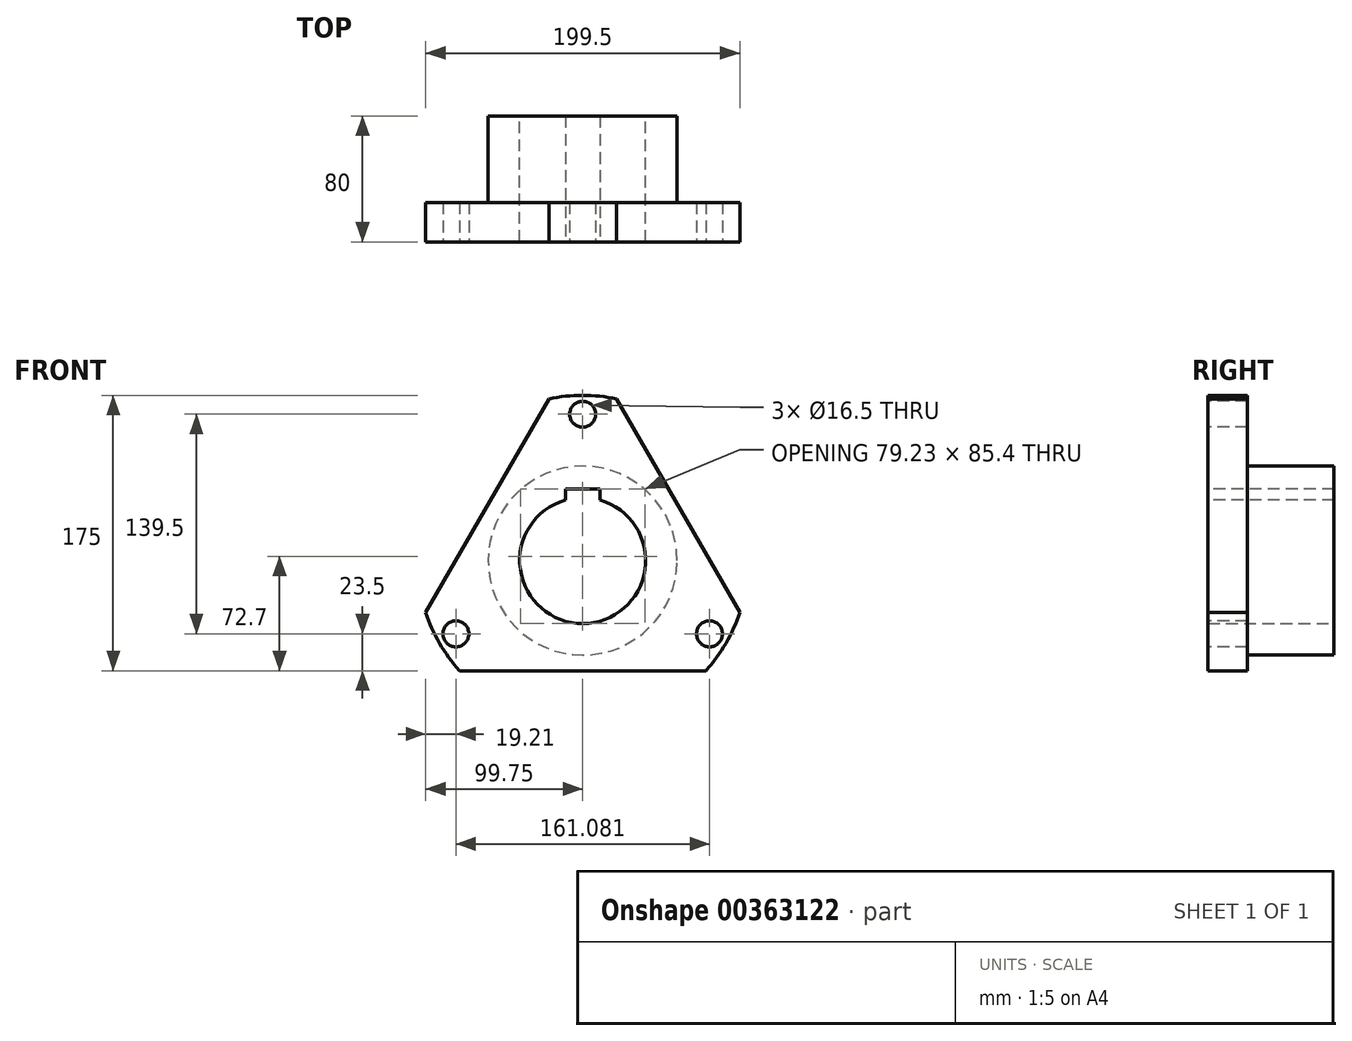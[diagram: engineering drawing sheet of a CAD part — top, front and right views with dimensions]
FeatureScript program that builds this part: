
annotation { "Feature Type Name" : "Feature", "Feature Type Description" : "" }
export const myFeature = defineFeature(function(context is Context, id is Id, definition is map)
    precondition{}
    {
        {
            var Q0;
            Q0=qCreatedBy(makeId("Front.planeOp"),FACE);
            var sketch = newSketch(context, id + "F0", { "sketchPlane" : qUnion([Q0])});
            skCircle(sketch, "E0", {"center": v(0, 0) * mm, "radius": 40 * mm});
            skCircle(sketch, "E1", {"center": v(0, 0) * mm, "radius": 60 * mm});
            skSolve(sketch);
        }
        {
            var Q0;
            Q0=qSketchRegion(id+"F0",true);
            extrude(context, id + "F1", {"entities" : qUnion([Q0]), "depth" : 80 * mm});
        }
        {
            var Q0;
            Q0=makeQuery(id+"F1.opExtrude","CAP_FACE",FACE,{"disambiguationData":[OSD([sQuery(id+"F0.wireOp",EDGE,"E0"),sQuery(id+"F0.wireOp",EDGE,"E1")])],"isStart":false});
            var sketch = newSketch(context, id + "F2", { "sketchPlane" : qUnion([Q0])});
            skCircle(sketch, "E2", {"center": v(0, 0) * mm, "radius": 105 * mm});
            skCircle(sketch, "E3", {"center": v(0, 0) * mm, "radius": 93 * mm, "construction": true});
            skCircle(sketch, "E4", {"center": v(0, 93) * mm, "radius": 8.25 * mm});
            skCircle(sketch, "E5.1.0", {"center": v(-80.54, -46.5) * mm, "radius": 8.25 * mm});
            skCircle(sketch, "E5.2.0", {"center": v(80.54, -46.5) * mm, "radius": 8.25 * mm});
            skLineSegment(sketch, "E6", {"start": v(-98.6, -61.27) * mm, "end": v(0, 109.5) * mm, "construction": true});
            skLineSegment(sketch, "E7", {"start": v(-99.75, -32.78) * mm, "end": v(-21.5, 102.78) * mm});
            skLineSegment(sketch, "E8.1.0", {"start": v(78.26, -70) * mm, "end": v(-78.26, -70) * mm});
            skLineSegment(sketch, "E8.2.0", {"start": v(21.5, 102.78) * mm, "end": v(99.75, -32.78) * mm});
            skSolve(sketch);
        }
        {
            var Q0;
            Q0=makeQuery(id+"F2.imprint","IMPRINT",FACE,{"disambiguationData":[TD([[makeQuery(id+"F2.imprint","IMPRINT",EDGE,{"derivedFrom":sQuery(id+"F2.wireOp",EDGE,"E4")}),-1.0]])]});
            var Q1;
            Q1=makeQuery(id+"F2.imprint","IMPRINT",FACE,{"disambiguationData":[TD([[makeQuery(id+"F2.imprint","IMPRINT",EDGE,{"derivedFrom":sQuery(id+"F2.wireOp",EDGE,"E5.1.0")}),-1.0]])]});
            var Q2;
            Q2=makeQuery(id+"F2.imprint","IMPRINT",FACE,{"disambiguationData":[TD([[makeQuery(id+"F2.imprint","IMPRINT",EDGE,{"derivedFrom":sQuery(id+"F2.wireOp",EDGE,"E5.2.0")}),-1.0]])]});
            extrude(context, id + "F3", {"entities" : qUnion([Q0, Q1, Q2]), "operationType" : NewBodyOperationType.ADD, "depth" : -25 * mm});
        }
        {
            var Q0;
            {var subQ0=sQuery(id+"F2.wireOp",EDGE,"E8.2.0");var subQ1=sQuery(id+"F2.wireOp",EDGE,"E8.1.0");var subQ2=sQuery(id+"F2.wireOp",EDGE,"E2");var subQ3=sQuery(id+"F0.wireOp",EDGE,"E1");var subQ4=sQuery(id+"F2.wireOp",EDGE,"E7");Q0=makeQuery(id+"F3.boolean.opBoolean","MERGE",FACE,{"derivedFrom":[makeQuery(id+"F1.opExtrude","CAP_FACE",FACE,{"disambiguationData":[OSD([sQuery(id+"F0.wireOp",EDGE,"E0"),subQ3])],"isStart":false}),makeQuery(id+"F3.opExtrude","CAP_FACE",FACE,{"disambiguationData":[OSD([subQ3,subQ2,sQuery(id+"F2.wireOp",EDGE,"E4"),subQ4,subQ0])],"isStart":true}),makeQuery(id+"F3.opExtrude","CAP_FACE",FACE,{"disambiguationData":[OSD([subQ3,subQ2,sQuery(id+"F2.wireOp",EDGE,"E5.1.0"),subQ4,subQ1])],"isStart":true}),makeQuery(id+"F3.opExtrude","CAP_FACE",FACE,{"disambiguationData":[OSD([subQ3,subQ2,sQuery(id+"F2.wireOp",EDGE,"E5.2.0"),subQ1,subQ0])],"isStart":true})]});}
            var sketch = newSketch(context, id + "F4", { "sketchPlane" : qUnion([Q0])});
            skLineSegment(sketch, "E9", {"start": v(-11, 45.4) * mm, "end": v(11, 45.4) * mm});
            skLineSegment(sketch, "E10", {"start": v(11, 45.4) * mm, "end": v(11, 38.46) * mm});
            skLineSegment(sketch, "E11", {"start": v(-11, 45.4) * mm, "end": v(-11, 38.46) * mm});
            skLineSegment(sketch, "E12", {"start": v(0, -78.52) * mm, "end": v(0, 108.67) * mm, "construction": true});
            skPoint(sketch, "E12.startSnap0", {"position": v(0, -70) * mm});
            skPoint(sketch, "E12.endSnap0", {"position": v(0, 105) * mm});
            skCircle(sketch, "E13.0", {"center": v(0, 0) * mm, "radius": 40 * mm});
            skSolve(sketch);
        }
        {
            var Q0;
            Q0=makeQuery(id+"F4.imprint","IMPRINT",FACE,{"disambiguationData":[TD([[makeQuery(id+"F4.imprint","IMPRINT",EDGE,{"derivedFrom":sQuery(id+"F4.wireOp",EDGE,"E9")}),-1.0]])]});
            extrude(context, id + "F5", {"entities" : qUnion([Q0]), "operationType" : NewBodyOperationType.REMOVE, "endBound" : BoundingType.THROUGH_ALL, "oppositeDirection" : true, "depth" : 25 * mm});
        }
    });
